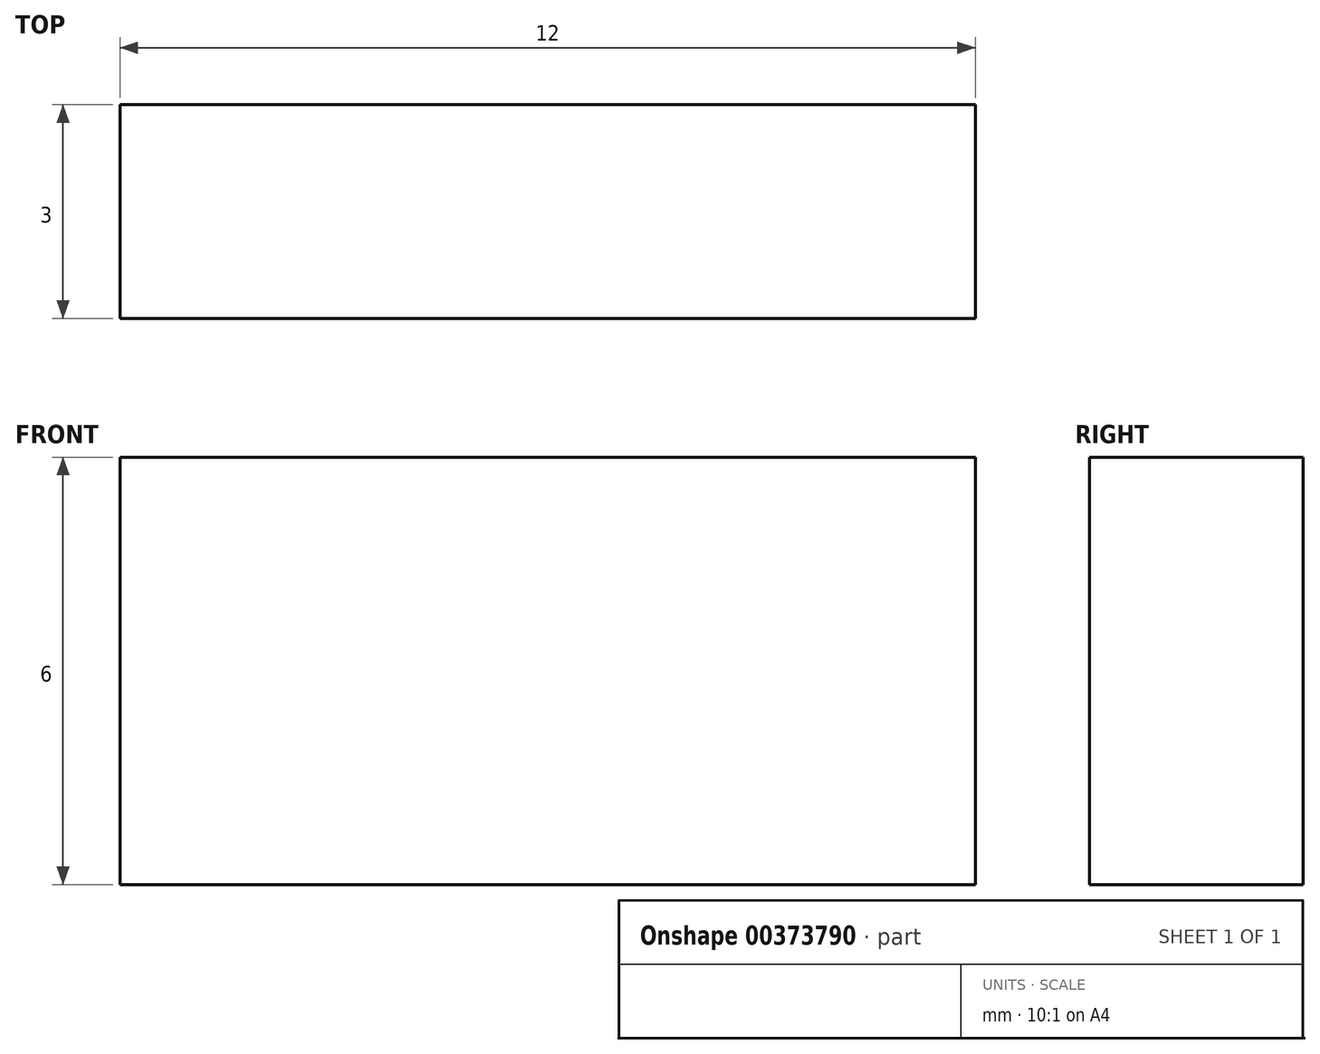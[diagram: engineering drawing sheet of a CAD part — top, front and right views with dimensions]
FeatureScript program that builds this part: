
annotation { "Feature Type Name" : "Feature", "Feature Type Description" : "" }
export const myFeature = defineFeature(function(context is Context, id is Id, definition is map)
    precondition{}
    {
        {
            var Q0;
            Q0=qCreatedBy(makeId("Front.planeOp"),FACE);
            var sketch = newSketch(context, id + "F0", { "sketchPlane" : qUnion([Q0])});
            skLineSegment(sketch, "E0.bottom", {"start": v(6, -3) * mm, "end": v(-6, -3) * mm});
            skLineSegment(sketch, "E0.top", {"start": v(6, 3) * mm, "end": v(-6, 3) * mm});
            skLineSegment(sketch, "E0.left", {"start": v(6, -3) * mm, "end": v(6, 3) * mm});
            skLineSegment(sketch, "E0.right", {"start": v(-6, -3) * mm, "end": v(-6, 3) * mm});
            skPoint(sketch, "E0.middle", {"position": v(0, 0) * mm});
            skSolve(sketch);
        }
        {
            var Q0;
            Q0=qSketchRegion(id+"F0",true);
            extrude(context, id + "F1", {"entities" : qUnion([Q0]), "depth" : 3 * mm});
        }
    });
